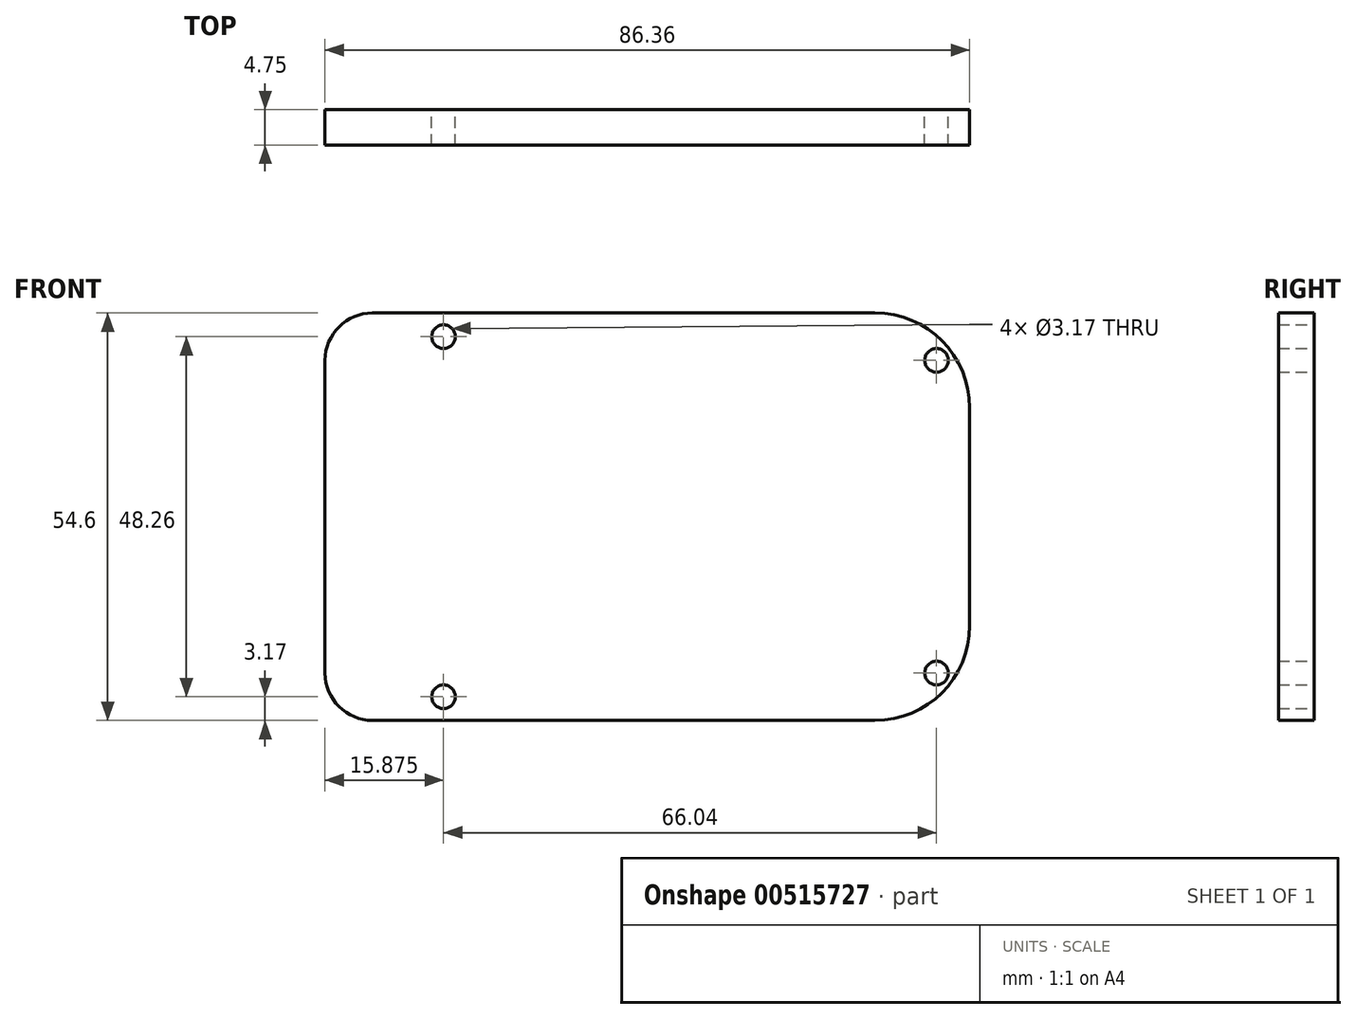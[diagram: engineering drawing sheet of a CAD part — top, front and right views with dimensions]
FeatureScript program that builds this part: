
annotation { "Feature Type Name" : "Feature", "Feature Type Description" : "" }
export const myFeature = defineFeature(function(context is Context, id is Id, definition is map)
    precondition{}
    {
        {
            var Q0;
            Q0=qCreatedBy(makeId("Front.planeOp"),FACE);
            var sketch = newSketch(context, id + "F0", { "sketchPlane" : qUnion([Q0])});
            skLineSegment(sketch, "E0.bottom", {"start": v(30.48, 27.3) * mm, "end": v(-36.83, 27.3) * mm});
            skLineSegment(sketch, "E0.top", {"start": v(30.48, -27.3) * mm, "end": v(-36.83, -27.3) * mm});
            skLineSegment(sketch, "E0.left", {"start": v(43.18, 14.6) * mm, "end": v(43.18, -14.6) * mm});
            skLineSegment(sketch, "E0.right", {"start": v(-43.18, 20.95) * mm, "end": v(-43.18, -20.96) * mm});
            skPoint(sketch, "E0.middle", {"position": v(0, 0) * mm});
            skCircle(sketch, "E1", {"center": v(-27.3, 24.13) * mm, "radius": 1.59 * mm});
            skCircle(sketch, "E2", {"center": v(-27.3, -24.13) * mm, "radius": 1.59 * mm});
            skCircle(sketch, "E3", {"center": v(38.74, 20.96) * mm, "radius": 1.59 * mm});
            skCircle(sketch, "E4", {"center": v(38.74, -20.96) * mm, "radius": 1.59 * mm});
            skPoint(sketch, "E5.visualSharp", {"position": v(-43.18, 27.3) * mm});
            skArc(sketch, "E5.filletArc", {"start": v(-36.83, 27.3) * mm, "mid": v(-41.32, 25.45) * mm, "end": v(-43.18, 20.95) * mm});
            skPoint(sketch, "E6.visualSharp", {"position": v(-43.18, -27.3) * mm});
            skArc(sketch, "E6.filletArc", {"start": v(-43.18, -20.96) * mm, "mid": v(-41.32, -25.45) * mm, "end": v(-36.83, -27.3) * mm});
            skPoint(sketch, "E7.visualSharp", {"position": v(43.18, 27.3) * mm});
            skArc(sketch, "E7.filletArc", {"start": v(43.18, 14.6) * mm, "mid": v(39.46, 23.59) * mm, "end": v(30.48, 27.3) * mm});
            skPoint(sketch, "E8.visualSharp", {"position": v(43.18, -27.3) * mm});
            skArc(sketch, "E8.filletArc", {"start": v(30.48, -27.3) * mm, "mid": v(39.46, -23.59) * mm, "end": v(43.18, -14.6) * mm});
            skSolve(sketch);
        }
        {
            var Q0;
            Q0 = qSketchRegion(id + "F0", true);
            extrude(context, id + "F1", {"entities" : qUnion([Q0]), "depth" : 4.75 * mm, "offsetDistance" : 25.4 * mm});
        }
    });
